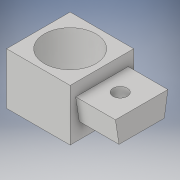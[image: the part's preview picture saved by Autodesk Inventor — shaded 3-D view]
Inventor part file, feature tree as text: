
AUTODESK INVENTOR PART (.ipt)
format: ipt  version: 2018 (Build 220112000, 112)  size: 122,880 bytes
history: native  units: in
note: dims shown in document units (in); Inventor stores cm internally (conversion verified against a paired STEP export)
features: extrude x3, sketch x3
ambient origin geometry x8: Origin, YZ Plane, XZ Plane, XY Plane, X Axis, Y Axis, Z Axis, Center Point
bodies: Solid1 (feature_tree)
feature tree (6):
  extrude  "Extrusion1"  Depth=0.8in
  extrude  "Extrusion2"  Depth=0.4in
  extrude  "Extrusion3"  Depth=0.65in TaperAngle=0.0deg
  sketch  "Sketch1"  dims[d0=0.8in d1=0.8in]
  sketch  "Sketch2"  dims[d2=0.4in d3=0.4in]
  sketch  "Sketch3"  dims[d4=0.65in d5=0.65in d6=0.0in d7=0.66in d8=0.57in d9=0.29in d10=0.2in d11=0.115in d12=0.5in d13=0.0in d14=0.18in d15=0.27in d16=0.7in d17=0.0in]
